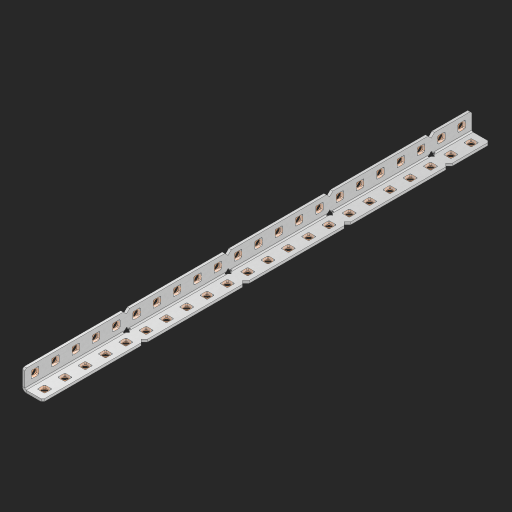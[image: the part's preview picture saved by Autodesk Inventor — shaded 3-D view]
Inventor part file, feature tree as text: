
AUTODESK INVENTOR PART (.ipt)
format: ipt  version: 2023 (Build 270158000, 158)  size: 852,480 bytes
history: native  units: in
note: dims shown in document units (in); Inventor stores cm internally (conversion verified against a paired STEP export)
features: other x50, extrude x45, sheet_metal_op x8, sketch x5, pattern_linear x1, mirror x1, chamfer x1
ambient origin geometry x8: Origin, YZ Plane, XZ Plane, XY Plane, X Axis, Y Axis, Z Axis, Center Point
bodies: Solid1 (feature_tree), Body (feature_tree)
feature tree (111):
  sheet_metal_op  "Flanges"
  sheet_metal_op  "Body Pattern"
  other  "Arc Length"
  pattern_linear  "Notch Pattern"  Spacing1=0.125in  [1 undecoded]
  other  "Diagonal Plane"
  mirror  "Everything Mirrored"
  chamfer  "End Chamfer"
  sketch  "Sketch1"  dims[d0=0.5in]
  other  "Plate1"
  sketch  "Sketch2"  dims[d1=11.0in]
  other  "Plate2"
  sheet_metal_op  "Bend1"
  sheet_metal_op  "Corner1"
  sketch  "Sketch8"  dims[d2=0.0625in]
  sketch  "Sketch9"  dims[d3=0.0625in]
  other  "Srf91"
  sheet_metal_op  "Body Pattern Sketch"
  other  "Srf92"
  sketch  "Sketch13"  dims[d4=0.0312in d5=0.125in d6=0.0625in d7=0.5in d8=90.0deg d9=0.0312in d10=0.25in d11=0.0625in d12=0.0625in d49=0.182in d50=0.02in d52=0.25in d53=0.0625in d54=0.0in d55=0.172in d56=1.0in d57=0.0in d85=0.1473in d86=0.1782in d89=0.0625in d90=0.0in d91=0.04in d92=0.0491in d95=2.5in d96=0.04in d97=0.25in d98=45.0deg d123=0.204in d126=0.0491in d127=0.1473in d128=0.08in d129=0.04in d130=2.5in d131=8.6614in d133=0.5in d134=0.3937in d136=1.0in]
  other  "Srf856"
  other  "Srf857"
  other  "Srf858"
  other  "Srf859"
  other  "Srf860"
  other  "Srf861"
  other  "Srf1275"
  other  "Srf1276"
  other  "Srf1278"
  other  "Srf1279"
  other  "Srf1280"
  other  "Srf1281"
  other  "Srf1282"
  other  "Srf1283"
  other  "Srf1383"
  other  "Srf1384"
  other  "Srf1385"
  other  "Srf1386"
  other  "Srf1387"
  other  "Srf1388"
  other  "Srf1389"
  other  "Srf1390"
  other  "Srf1391"
  other  "Srf1392"
  other  "Srf1393"
  other  "Srf1394"
  other  "Srf1395"
  other  "Srf1396"
  other  "Srf1397"
  other  "Srf1475"
  other  "Srf1476"
  other  "Srf1477"
  other  "Srf1478"
  other  "Srf1479"
  other  "Srf1480"
  other  "Srf1481"
  other  "Srf1482"
  other  "Srf1483"
  other  "Srf1484"
  other  "Srf1485"
  other  "Srf1486"
  other  "Srf1487"
  other  "Srf1488"
  other  "Srf1489"
  sheet_metal_op  "Body Stamp"
  sheet_metal_op  "Body Circle"
  sheet_metal_op  "Notch"
  extrude  "ExtrusionSrf92"  Depth=0.0625in
  extrude  "ExtrusionSrf856"  Depth=0.5in TaperAngle=90.0deg
  extrude  "ExtrusionSrf857"  Depth=0.25in
  extrude  "ExtrusionSrf858"  Depth=0.0625in
  extrude  "ExtrusionSrf859"  Depth=0.0625in
  extrude  "ExtrusionSrf860"  Depth=0.3937in
  extrude  "ExtrusionSrf861"  Depth=0.02in
  extrude  "ExtrusionSrf1275"  Depth=0.25in
  extrude  "ExtrusionSrf1276"  Depth=0.0625in
  extrude  "ExtrusionSrf1277"  TaperAngle=0.0deg  [1 undecoded]
  extrude  "ExtrusionSrf1278"  Depth=0.3937in
  extrude  "ExtrusionSrf1279"  Depth=0.3937in TaperAngle=0.0deg
  extrude  "ExtrusionSrf1280"  Depth=0.3937in
  extrude  "ExtrusionSrf1281"  Depth=0.3937in
  extrude  "ExtrusionSrf1282"  Depth=0.0625in
  extrude  "ExtrusionSrf1383"  Depth=0.3937in TaperAngle=0.0deg
  extrude  "ExtrusionSrf1384"  Depth=0.3937in
  extrude  "ExtrusionSrf1385"  Depth=0.25in TaperAngle=45.0deg
  extrude  "ExtrusionSrf1386"  Depth=0.3937in
  extrude  "ExtrusionSrf1387"  Depth=0.3937in
  extrude  "ExtrusionSrf1388"  Depth=0.3937in
  extrude  "ExtrusionSrf1389"  Depth=0.3937in
  extrude  "ExtrusionSrf1390"  Depth=0.3937in
  extrude  "ExtrusionSrf1391"  Depth=0.3937in
  extrude  "ExtrusionSrf1392"  Depth=0.3937in
  extrude  "ExtrusionSrf1393"  Depth=0.5in
  extrude  "ExtrusionSrf1394"  [1 undecoded]
  extrude  "ExtrusionSrf1395"  [1 undecoded]
  extrude  "ExtrusionSrf1396"  [1 undecoded]
  extrude  "ExtrusionSrf1397"  [1 undecoded]
  extrude  "ExtrusionSrf1475"  [1 undecoded]
  extrude  "ExtrusionSrf1476"  [1 undecoded]
  extrude  "ExtrusionSrf1477"  [1 undecoded]
  extrude  "ExtrusionSrf1478"  [1 undecoded]
  extrude  "ExtrusionSrf1479"  [1 undecoded]
  extrude  "ExtrusionSrf1480"  [1 undecoded]
  extrude  "ExtrusionSrf1481"  [1 undecoded]
  extrude  "ExtrusionSrf1482"  [1 undecoded]
  extrude  "ExtrusionSrf1483"  [1 undecoded]
  extrude  "ExtrusionSrf1484"  [1 undecoded]
  extrude  "ExtrusionSrf1485"  [1 undecoded]
  extrude  "ExtrusionSrf1486"  [1 undecoded]
  extrude  "ExtrusionSrf1487"  [1 undecoded]
  extrude  "ExtrusionSrf1488"  [1 undecoded]
  extrude  "ExtrusionSrf1489"  [1 undecoded]
note: 21 required parameter values undecoded (feature->parameter linkage not recoverable at this tier; creation-order binding heuristic only, values carry confidence <= 0.55)
